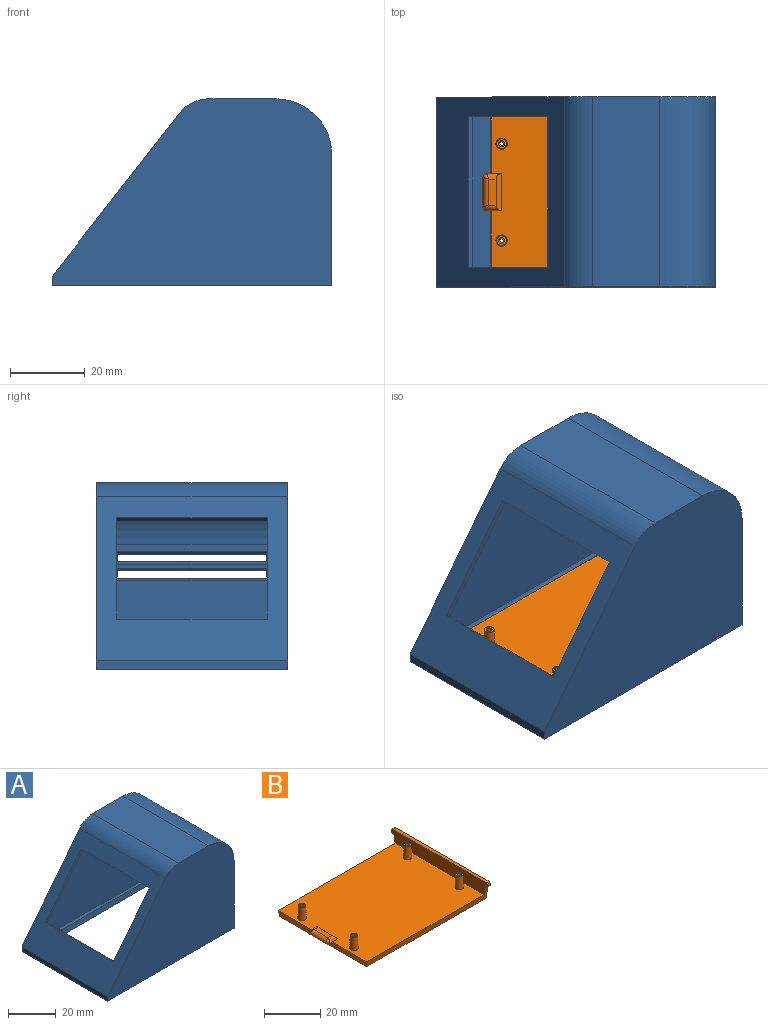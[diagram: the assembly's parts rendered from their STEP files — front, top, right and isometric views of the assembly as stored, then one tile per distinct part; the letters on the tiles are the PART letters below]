
ASSEMBLY  parts=2 mates=1
PART A: 53 faces, bbox 75x51x50 mm
  f0: plane 3.58x1.57mm, normal (-1,0,0), area 4.5mm2, adj f2,f6,f8,f52
  f1: plane 3.58x1.57mm, normal (-1,0,0), area 4.5mm2, adj f3,f6,f7,f51
  f2: plane 60.43x6mm, normal (0,0.98,0.17), area 153.6mm2, adj f0,f4,f6,f14,f26,f52
  f3: plane 60.43x6mm, normal (0,-0.98,0.17), area 153.6mm2, adj f1,f4,f6,f14,f26,f51
  f4: plane 51x35mm, normal (1,0,0), area 1258.7mm2, adj f2,f3,f7,f8,f13,f14,f15,f16
  f5: plane 48x25.5mm, normal (-1,0,0), area 942.6mm2, adj f7,f8,f24,f25,f27,f28,f29,f30
  f6: plane 71.61x48mm, normal (0,0,1), area 794mm2, adj f0,f1,f2,f3,f7,f8,f10,f26
  f7: plane 73.11x46.08mm, normal (0,-1,0), area 2421.4mm2, adj f1,f4,f5,f6,f10,f18,f19,f24
  f8: plane 73.11x46.08mm, normal (0,1,0), area 2421.4mm2, adj f0,f4,f5,f6,f10,f18,f19,f24
  f9: plane 51x43.91mm, normal (-0.79,0,0.62), area 1444.9mm2, adj f11,f13,f15,f17,f20,f21,f22,f23
  f10: plane 48x42.23mm, normal (0.79,0,-0.62), area 1148.9mm2, adj f6,f7,f8,f18,f20,f21,f22,f23
  f11: plane 51x2.42mm, normal (-1,0,0), area 123.6mm2, adj f9,f13,f14,f15
  f12: plane 51x17.96mm, normal (0,0,1), area 915.7mm2, adj f13,f15,f16,f17
  f13: plane 75x50mm, normal (0,1,0), area 2814.1mm2, adj f4,f9,f11,f12,f14,f16,f17
  f14: plane 75x51mm, normal (0,0,-1), area 1185mm2, adj f2,f3,f4,f11,f13,f15,f26
  f15: plane 75x50mm, normal (0,-1,0), area 2814.1mm2, adj f4,f9,f11,f12,f14,f16,f17
  f16: cylinder r=15mm len=51mm, axis (0,-1,0), area 1201.7mm2, adj f4,f12,f13,f15
  f17: cylinder r=10mm len=51mm, axis (0,-1,0), area 451mm2, adj f9,f12,f13,f15
  f18: cylinder r=10mm len=48mm, axis (0,-1,0), area 435.6mm2, adj f7,f8,f10,f19
  f19: plane 48x15.73mm, normal (0,0,-1), area 755.1mm2, adj f7,f8,f18,f24
  f20: plane 40.5x1.18mm, normal (-0.62,0,-0.79), area 60.4mm2, adj f9,f10,f21,f23
  f21: plane 28.11x22.42mm, normal (0,-1,0), area 51.5mm2, adj f9,f10,f20,f22
  f22: plane 40.5x1.18mm, normal (0.62,0,0.79), area 60.4mm2, adj f9,f10,f21,f23
  f23: plane 28.11x22.42mm, normal (0,1,0), area 51.5mm2, adj f9,f10,f20,f22
  f24: cylinder r=15mm len=48mm, axis (0,-1,0), area 1131mm2, adj f5,f7,f8,f19
  f25: plane 48x1.5mm, normal (0,0,-1), area 72mm2, adj f4,f5,f7,f8
  f26: plane 44.85x2.42mm, normal (0.98,0,0.17), area 109.3mm2, adj f2,f3,f6,f14
  f27: plane 3.4x1.5mm, normal (-0.42,0.91,0), area 4.5mm2, adj f4,f5,f28,f29
  f28: plane 41.4x1.5mm, normal (-0.42,0,-0.91), area 67.4mm2, adj f4,f5,f27,f30
  f29: plane 41.4x1.5mm, normal (-0.42,0,0.91), area 67.4mm2, adj f4,f5,f27,f30
  f30: plane 3.4x1.5mm, normal (-0.42,-0.91,0), area 4.5mm2, adj f4,f5,f28,f29
  f31: plane 3.4x1.5mm, normal (-0.42,0.91,0), area 4.5mm2, adj f4,f5,f32,f33
  f32: plane 41.4x1.5mm, normal (-0.42,0,-0.91), area 67.4mm2, adj f4,f5,f31,f34
  f33: plane 41.4x1.5mm, normal (-0.42,0,0.91), area 67.4mm2, adj f4,f5,f31,f34
  f34: plane 3.4x1.5mm, normal (-0.42,-0.91,0), area 4.5mm2, adj f4,f5,f32,f33
  f35: cone r=0.5mm half-angle=7deg, axis (0.79,0,-0.62), area 7.9mm2, adj f37,f38
  f36: cone r=1.45mm half-angle=7deg, axis (-0.79,0,0.62), area 16.8mm2, adj f10,f37
  f37: plane 2.41x1.9mm, normal (0.79,0,-0.62), area 2.8mm2, adj f35,f36
  f38: plane 1x0.79mm, normal (0.79,0,-0.62), area 0.8mm2, adj f35
  f39: cone r=0.5mm half-angle=7deg, axis (0.79,0,-0.62), area 7.9mm2, adj f41,f42
  f40: cone r=1.45mm half-angle=7deg, axis (-0.79,0,0.62), area 16.8mm2, adj f10,f41
  f41: plane 2.41x1.9mm, normal (0.79,0,-0.62), area 2.8mm2, adj f39,f40
  f42: plane 1x0.79mm, normal (0.79,0,-0.62), area 0.8mm2, adj f39
  f43: cone r=0.5mm half-angle=7deg, axis (0.79,0,-0.62), area 7.9mm2, adj f45,f46
  f44: cone r=1.45mm half-angle=7deg, axis (-0.79,0,0.62), area 16.8mm2, adj f10,f45
  f45: plane 2.41x1.9mm, normal (0.79,0,-0.62), area 2.8mm2, adj f43,f44
  f46: plane 1x0.79mm, normal (0.79,0,-0.62), area 0.8mm2, adj f43
  f47: cone r=0.5mm half-angle=7deg, axis (0.79,0,-0.62), area 7.9mm2, adj f49,f50
  f48: cone r=1.45mm half-angle=7deg, axis (-0.79,0,0.62), area 16.8mm2, adj f10,f49
  f49: plane 2.41x1.9mm, normal (0.79,0,-0.62), area 2.8mm2, adj f47,f48
  f50: plane 1x0.79mm, normal (0.79,0,-0.62), area 0.8mm2, adj f47
  f51: plane 1.5x0.94mm, normal (0,0,1), area 1.4mm2, adj f1,f3,f4,f7
  f52: plane 1.5x0.94mm, normal (0,0,1), area 1.4mm2, adj f0,f2,f4,f8
PART B: 40 faces, bbox 62.5x47.8x8 mm
  f0: plane 58.75x44.68mm, normal (0,0,1), area 2568.9mm2, adj f2,f3,f4,f6,f17,f20,f22,f25
  f1: plane 46.8x1.45mm, normal (0,0,1), area 67.9mm2, adj f6,f7,f12,f15
  f2: plane 60.2x6.1mm, normal (0,0.98,-0.17), area 157.6mm2, adj f0,f3,f5,f6,f7,f10
  f3: plane 44.68x2.5mm, normal (-0.98,0,-0.17), area 112.3mm2, adj f0,f2,f4,f5,f32
  f4: plane 60.2x6.1mm, normal (0,-0.98,-0.17), area 157.6mm2, adj f0,f3,f5,f6,f7,f9
  f5: plane 59.76x43.8mm, normal (0,0,-1), area 2589.2mm2, adj f2,f3,f4,f7,f28,f29,f30,f31
  f6: plane 47.8x5.5mm, normal (-1,0,0), area 253.7mm2, adj f0,f1,f2,f4,f8,f9,f10,f11
  f7: plane 47.8x8mm, normal (1,0,0), area 364.3mm2, adj f1,f2,f4,f5,f8,f9,f10,f11
  f8: plane 1.45x0.9mm, normal (0,-1,0), area 1.3mm2, adj f6,f7,f12,f13
  f9: plane 1.45x0.42mm, normal (0,0,-1), area 0.6mm2, adj f4,f6,f7,f13
  f10: plane 1.45x0.42mm, normal (0,0,-1), area 0.6mm2, adj f2,f6,f7,f14
  f11: plane 1.45x0.9mm, normal (0,1,0), area 1.3mm2, adj f6,f7,f14,f15
  f12: cylinder r=0.5mm len=1.45mm, axis (1,0,0), area 1.1mm2, adj f1,f6,f7,f8
  f13: cylinder r=0.5mm len=1.45mm, axis (1,0,0), area 1.1mm2, adj f6,f7,f8,f9
  f14: cylinder r=0.5mm len=1.45mm, axis (-1,0,0), area 1.1mm2, adj f6,f7,f10,f11
  f15: cylinder r=0.5mm len=1.45mm, axis (-1,0,0), area 1.1mm2, adj f1,f6,f7,f11
  f16: cone r=0.5mm half-angle=2deg, axis (0,0,1), area 28.9mm2, adj f18,f29
  f17: cone r=1.6mm half-angle=2deg, axis (0,0,-1), area 49mm2, adj f0,f18
  f18: plane 2.64x2.64mm, normal (0,0,1), area 3.6mm2, adj f16,f17
  f19: cone r=0.5mm half-angle=2deg, axis (0,0,1), area 28.9mm2, adj f21,f28
  f20: cone r=1.6mm half-angle=2deg, axis (0,0,-1), area 49mm2, adj f0,f21
  f21: plane 2.64x2.64mm, normal (0,0,1), area 3.6mm2, adj f19,f20
  f22: cone r=1.6mm half-angle=2deg, axis (0,0,-1), area 49mm2, adj f0,f24
  f23: cone r=0.5mm half-angle=2deg, axis (0,0,1), area 28.9mm2, adj f24,f31
  f24: plane 2.64x2.64mm, normal (0,0,1), area 3.6mm2, adj f22,f23
  f25: cone r=1.6mm half-angle=2deg, axis (0,0,-1), area 49mm2, adj f0,f27
  f26: cone r=0.5mm half-angle=2deg, axis (0,0,1), area 28.9mm2, adj f27,f30
  f27: plane 2.64x2.64mm, normal (0,0,1), area 3.6mm2, adj f25,f26
  f28: cone r=1.5mm half-angle=44deg, axis (0,0,-1), area 8.9mm2, adj f5,f19
  f29: cone r=1.5mm half-angle=44deg, axis (0,0,-1), area 8.9mm2, adj f5,f16
  f30: cone r=0.53mm half-angle=44deg, axis (0,0,-1), area 8.9mm2, adj f5,f26
  f31: cone r=0.53mm half-angle=44deg, axis (0,0,-1), area 8.9mm2, adj f5,f23
  f32: plane 10x2.26mm, normal (0,0,-1), area 22.2mm2, adj f3,f34,f35,f36,f37,f38
  f33: plane 7x2mm, normal (0,0,1), area 14mm2, adj f34,f36,f38,f39
  f34: cylinder r=1.5mm len=4mm, axis (-1,0,0), area 6.7mm2, adj f0,f32,f33,f35,f39
  f35: bspline ~1.82x1.5mm, area 2.4mm2, adj f32,f34,f36
  f36: cylinder r=1.5mm len=8mm, axis (0,1,0), area 18mm2, adj f32,f33,f35,f37
  f37: bspline ~1.82x1.5mm, area 2.4mm2, adj f32,f36,f38
  f38: cylinder r=1.5mm len=4mm, axis (1,0,0), area 6.7mm2, adj f0,f32,f33,f37,f39
  f39: plane 10x1.5mm, normal (0.71,0,0.71), area 19.8mm2, adj f0,f33,f34,f38
PLACE A t=(-7.27,0.02,-4.04)mm fixed
PLACE B t=(-7.23,0.02,-4.04)mm
MATE slider B.f7 <-> A.f4  axis (1,0,0) through (30.23,0.02,3.96)mm
